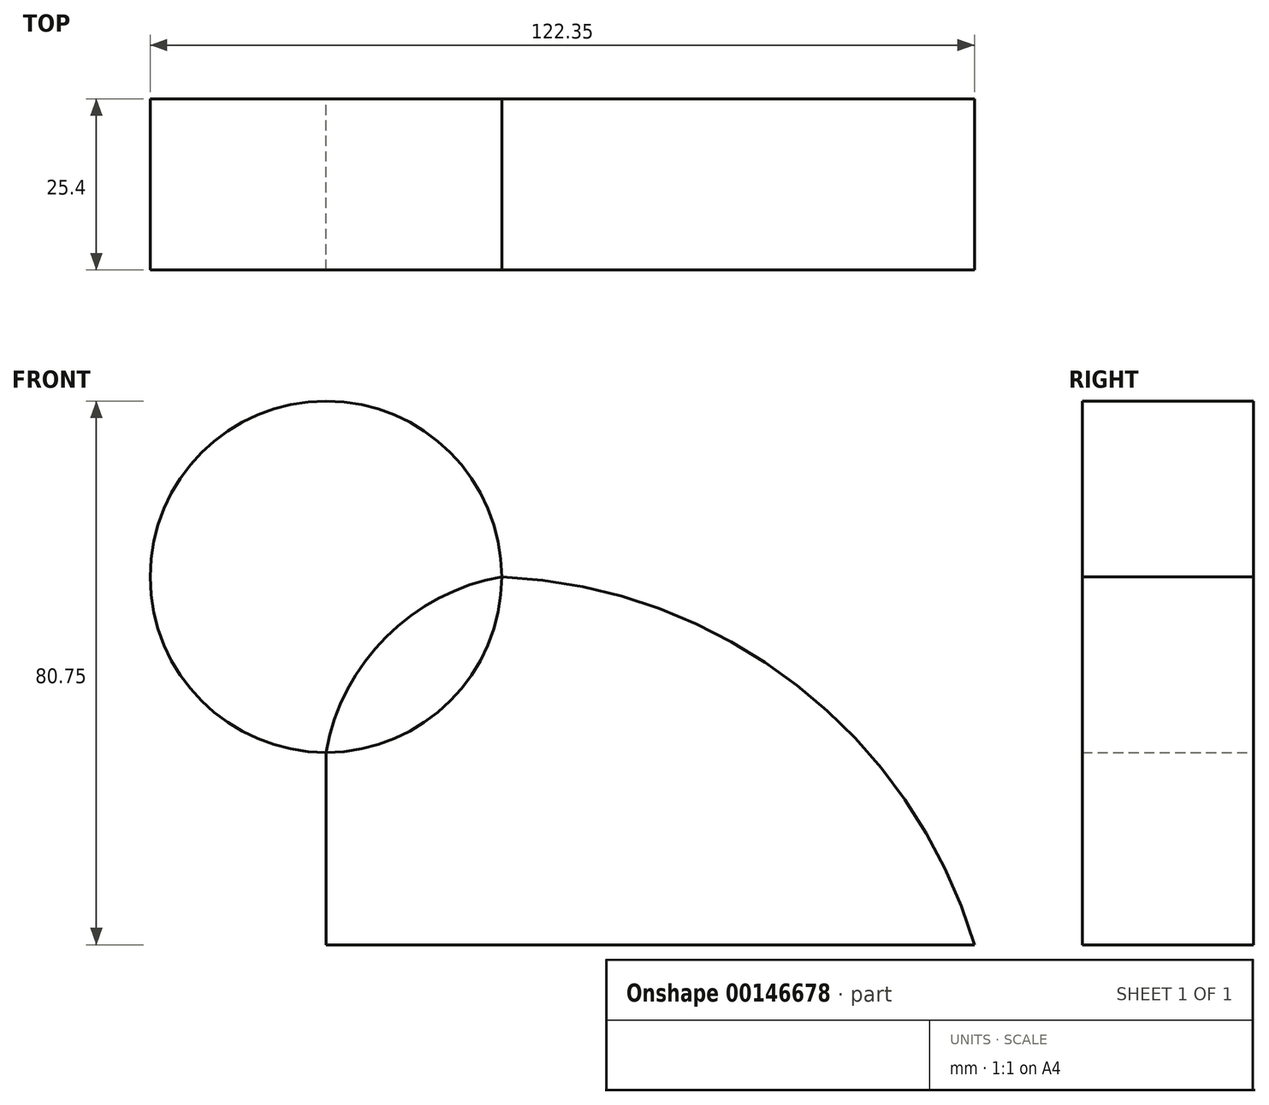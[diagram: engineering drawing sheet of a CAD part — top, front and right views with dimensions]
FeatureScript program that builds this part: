
annotation { "Feature Type Name" : "Feature", "Feature Type Description" : "" }
export const myFeature = defineFeature(function(context is Context, id is Id, definition is map)
    precondition{}
    {
        {
            var Q0;
            Q0=qCreatedBy(makeId("Front.planeOp"),FACE);
            var sketch = newSketch(context, id + "F0", { "sketchPlane" : qUnion([Q0])});
            skLineSegment(sketch, "E0.bottom", {"start": v(49.73, -27.33) * mm, "end": v(-49.73, -27.33) * mm});
            skLineSegment(sketch, "E0.top", {"start": v(49.73, 27.33) * mm, "end": v(-49.73, 27.33) * mm});
            skLineSegment(sketch, "E0.left", {"start": v(49.73, -27.33) * mm, "end": v(49.73, 27.33) * mm});
            skLineSegment(sketch, "E0.right", {"start": v(-49.73, -27.33) * mm, "end": v(-49.73, 27.33) * mm});
            skPoint(sketch, "E0.middle", {"position": v(0, 0) * mm});
            skCircle(sketch, "E1", {"center": v(-49.73, 27.33) * mm, "radius": 26.1 * mm});
            skSolve(sketch);
        }
        {
            var Q0;
            {var subQ0=sQuery(id+"F0.wireOp",EDGE,"E0.right");var subQ1=sQuery(id+"F0.wireOp",EDGE,"E0.top");var subQ2=makeQuery(id+"F0.imprint","INTERSECT",VERTEX,{"derivedFrom":[subQ1,subQ0]});Q0=makeQuery(id+"F0.imprint","IMPRINT",FACE,{"disambiguationData":[TD([[makeQuery(id+"F0.imprint","IMPRINT",EDGE,{"disambiguationData":[TD([[subQ2,1.0]])],"derivedFrom":subQ1}),-1.0]])]});}
            var Q1;
            {var subQ1=sQuery(id+"F0.wireOp",EDGE,"E0.bottom");Q1=makeQuery(id+"F0.imprint","IMPRINT",FACE,{"disambiguationData":[TD([[makeQuery(id+"F0.imprint","IMPRINT",EDGE,{"derivedFrom":subQ1}),-1.0]])]});}
            extrude(context, id + "F1", {"entities" : qUnion([Q0, Q1]), "depth" : 25.4 * mm});
        }
        {
            var Q0;
            Q0=makeQuery(id+"F1.opExtrude","SWEPT_EDGE",EDGE,{"disambiguationData":[OSD([sQuery(id+"F0.wireOp",EDGE,"E0.top"),sQuery(id+"F0.wireOp",EDGE,"E0.left")])]});
            fillet(context, id + "F2", {"entities" : qUnion([Q0]), "radius" : 76.65 * mm, "tangentPropagation" : true, "allowEdgeOverflow" : false});
        }
        {
            var Q0;
            Q0=makeQuery(id+"F1.opExtrude","SWEPT_EDGE",EDGE,{"disambiguationData":[OSD([sQuery(id+"F0.wireOp",EDGE,"E0.top"),sQuery(id+"F0.wireOp",EDGE,"E0.right")])]});
            fillet(context, id + "F3", {"entities" : qUnion([Q0]), "radius" : 32.2 * mm, "tangentPropagation" : true, "allowEdgeOverflow" : false});
        }
    });
